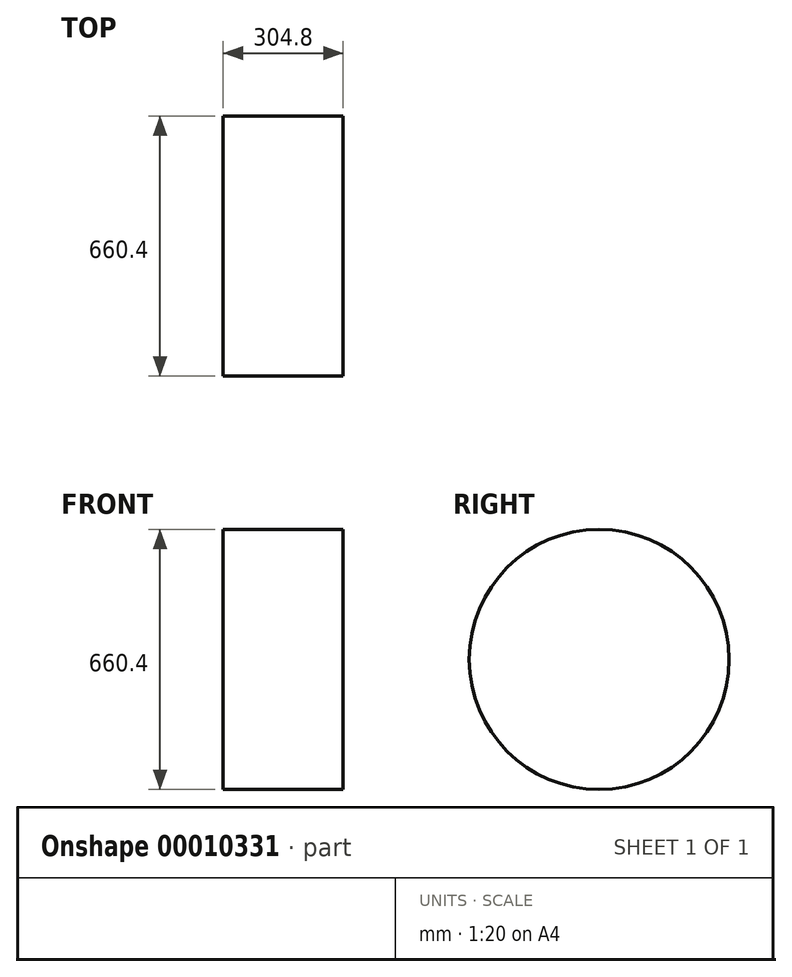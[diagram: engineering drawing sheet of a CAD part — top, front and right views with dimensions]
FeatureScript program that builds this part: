
annotation { "Feature Type Name" : "Feature", "Feature Type Description" : "" }
export const myFeature = defineFeature(function(context is Context, id is Id, definition is map)
    precondition{}
    {
        {
            var Q0;
            Q0=qCreatedBy(makeId("Right.planeOp"),FACE);
            var sketch = newSketch(context, id + "F0", { "sketchPlane" : qUnion([Q0])});
            skCircle(sketch, "E0", {"center": v(0, 0) * mm, "radius": 330.2 * mm});
            skSolve(sketch);
        }
        {
            var Q0;
            Q0=makeQuery(id+"F0.imprint","IMPRINT",FACE,{"disambiguationData":[TD([[makeQuery(id+"F0.imprint","IMPRINT",EDGE,{"derivedFrom":sQuery(id+"F0.wireOp",EDGE,"E0")}),1.0]])]});
            extrude(context, id + "F1", {"entities" : qUnion([Q0]), "depth" : 304.8 * mm});
        }
    });
